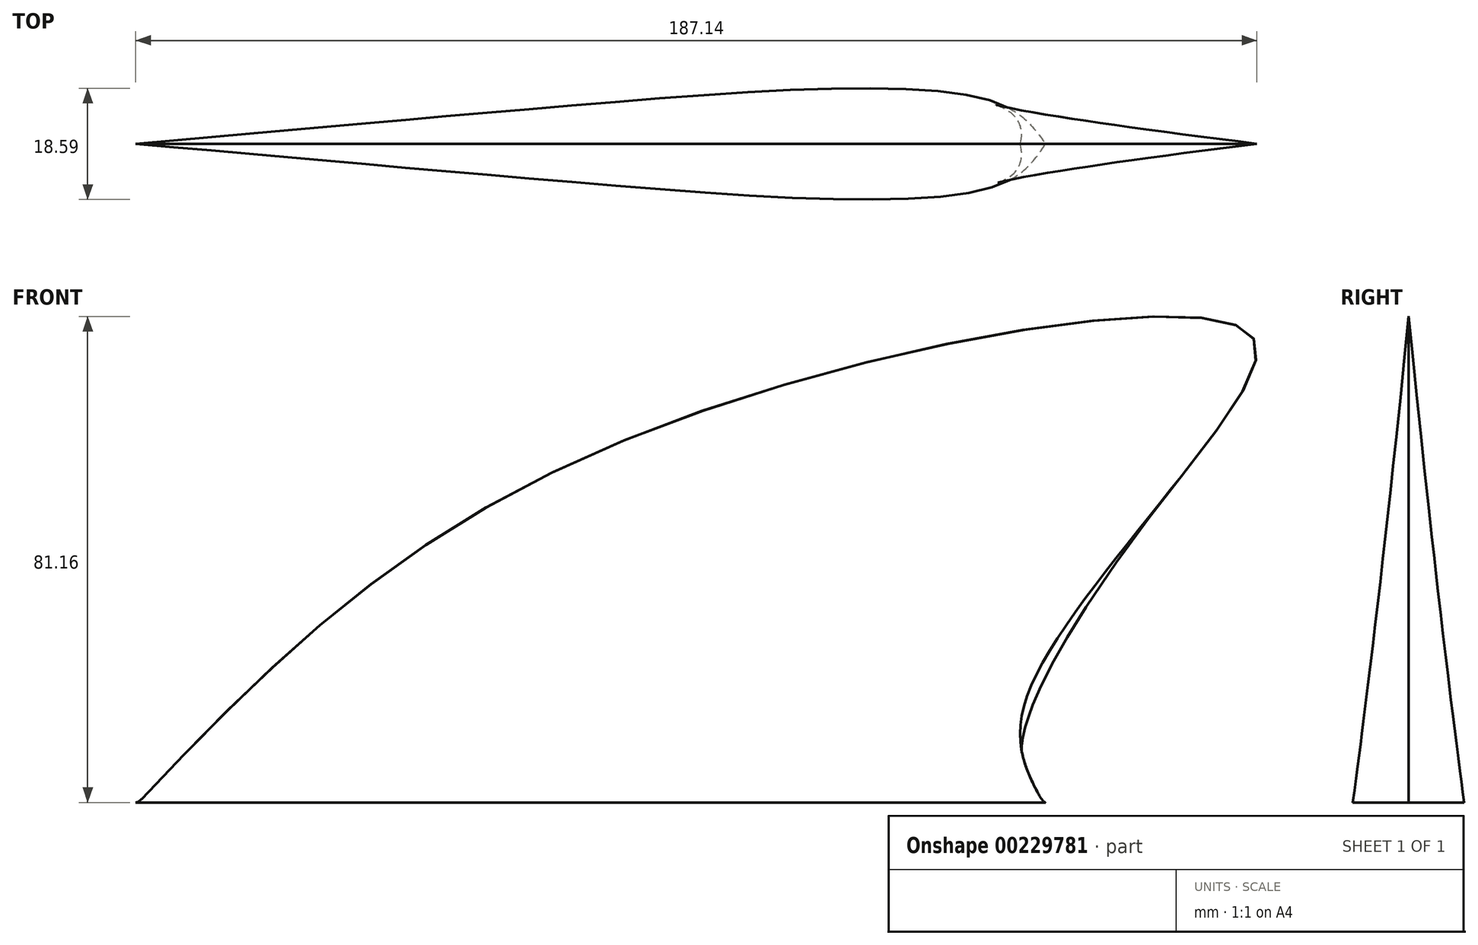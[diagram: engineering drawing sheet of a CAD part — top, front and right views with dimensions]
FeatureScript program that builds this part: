
annotation { "Feature Type Name" : "Feature", "Feature Type Description" : "" }
export const myFeature = defineFeature(function(context is Context, id is Id, definition is map)
    precondition{}
    {
        {
            var Q0;
            Q0=qCreatedBy(makeId("Top.planeOp"),FACE);
            var sketch = newSketch(context, id + "F0", { "sketchPlane" : qUnion([Q0])});
            skFitSpline(sketch, "E0", {"points": [v(-75.93, 0) * mm, v(0, 6.64) * mm, v(67.22, 7.05) * mm, v(75.93, 0) * mm], "startDerivative": vector(167.84, 15.1) * mm, "endDerivative": vector(35.16, -49.1) * mm});
            skSolve(sketch);
        }
        {
            var Q0;
            Q0=qCreatedBy(makeId("Top.planeOp"),FACE);
            var sketch = newSketch(context, id + "F1", { "sketchPlane" : qUnion([Q0])});
            skFitSpline(sketch, "E1", {"points": [v(-75.93, 0) * mm, v(0, -6.64) * mm, v(67.63, -7.05) * mm, v(75.93, 0) * mm], "startDerivative": vector(167.23, -15) * mm, "endDerivative": vector(33.17, 49.69) * mm});
            skSolve(sketch);
        }
        {
            var Q0;
            Q0=qCreatedBy(makeId("Front.planeOp"),FACE);
            var sketch = newSketch(context, id + "F2", { "sketchPlane" : qUnion([Q0])});
            skFitSpline(sketch, "E2", {"points": [v(-75.51, 0) * mm, v(0, 58.09) * mm, v(106.63, 80.08) * mm, v(110.37, 71.78) * mm, v(73.02, 18.26) * mm, v(75.51, 0) * mm], "startDerivative": vector(221.98, 232.91) * mm, "endDerivative": vector(69.3, -125.85) * mm});
            skSolve(sketch);
        }
        {
            var Q0;
            Q0=sQuery(id+"F1.wireOp",EDGE,"E1");
            var Q1;
            Q1=sQuery(id+"F2.wireOp",EDGE,"E2");
            loft(context, id + "F3", {"bodyType" : ToolBodyType.SURFACE, "wireProfilesArray" : [{ "wireProfileEntities" : qUnion([Q0]) }, { "wireProfileEntities" : qUnion([Q1]) }]});
        }
        {
            var Q0;
            Q0=sQuery(id+"F0.wireOp",EDGE,"E0");
            var Q1;
            Q1=sQuery(id+"F2.wireOp",EDGE,"E2");
            loft(context, id + "F4", {"bodyType" : ToolBodyType.SURFACE, "wireProfilesArray" : [{ "wireProfileEntities" : qUnion([Q0]) }, { "wireProfileEntities" : qUnion([Q1]) }]});
        }
    });
